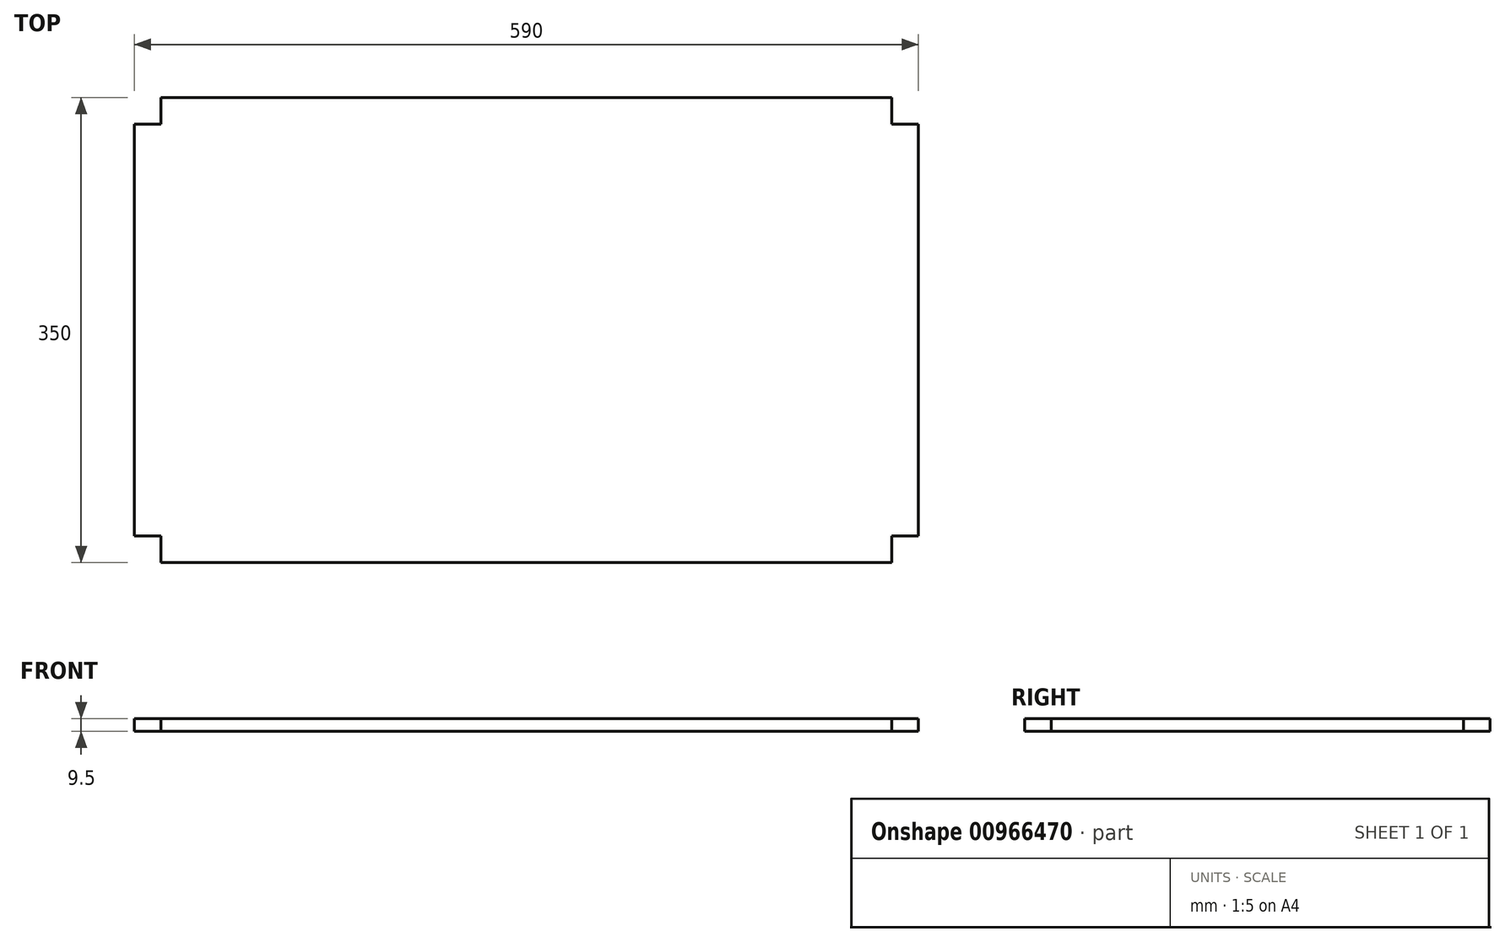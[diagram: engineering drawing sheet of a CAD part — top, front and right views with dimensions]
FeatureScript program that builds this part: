
annotation { "Feature Type Name" : "Feature", "Feature Type Description" : "" }
export const myFeature = defineFeature(function(context is Context, id is Id, definition is map)
    precondition{}
    {
        {
            var Q0;
            Q0=qCreatedBy(makeId("Top.planeOp"),FACE);
            var sketch = newSketch(context, id + "F0", { "sketchPlane" : qUnion([Q0])});
            skLineSegment(sketch, "E0.bottom", {"start": v(275, 175) * mm, "end": v(-275, 175) * mm});
            skLineSegment(sketch, "E0.top", {"start": v(275, -175) * mm, "end": v(-275, -175) * mm});
            skLineSegment(sketch, "E0.left", {"start": v(295, 155) * mm, "end": v(295, -155) * mm});
            skLineSegment(sketch, "E0.right", {"start": v(-295, 155) * mm, "end": v(-295, -155) * mm});
            skPoint(sketch, "E0.middle", {"position": v(0, 0) * mm});
            skLineSegment(sketch, "E1.top", {"start": v(-295, 155) * mm, "end": v(-275, 155) * mm});
            skLineSegment(sketch, "E1.right", {"start": v(-275, 175) * mm, "end": v(-275, 155) * mm});
            skLineSegment(sketch, "E2.top", {"start": v(295, 155) * mm, "end": v(275, 155) * mm});
            skLineSegment(sketch, "E2.right", {"start": v(275, 175) * mm, "end": v(275, 155) * mm});
            skLineSegment(sketch, "E3.top", {"start": v(295, -155) * mm, "end": v(275, -155) * mm});
            skLineSegment(sketch, "E3.right", {"start": v(275, -175) * mm, "end": v(275, -155) * mm});
            skLineSegment(sketch, "E4.top", {"start": v(-295, -155) * mm, "end": v(-275, -155) * mm});
            skLineSegment(sketch, "E4.right", {"start": v(-275, -175) * mm, "end": v(-275, -155) * mm});
            skPoint(sketch, "E5.orphan", {"position": v(-295, 175) * mm});
            skPoint(sketch, "E2.bottom.start.orphan", {"position": v(295, 175) * mm});
            skPoint(sketch, "E6.orphan", {"position": v(-295, -175) * mm});
            skPoint(sketch, "E7.orphan", {"position": v(295, -175) * mm});
            skSolve(sketch);
        }
        {
            var Q0;
            Q0 = qSketchRegion(id + "F0", true);
            extrude(context, id + "F1", {"entities" : qUnion([Q0]), "depth" : 9.5 * mm, "offsetDistance" : 25 * mm});
        }
    });
